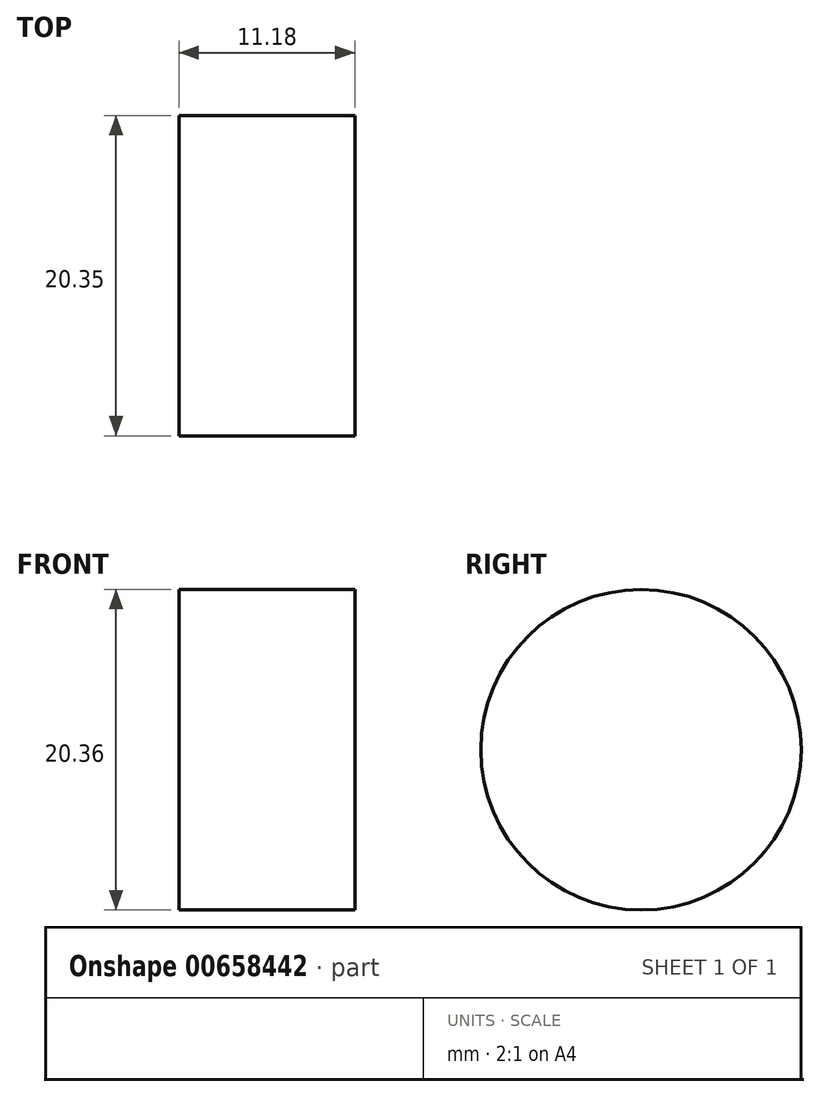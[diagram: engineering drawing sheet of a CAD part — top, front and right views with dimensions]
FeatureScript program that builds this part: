
annotation { "Feature Type Name" : "Feature", "Feature Type Description" : "" }
export const myFeature = defineFeature(function(context is Context, id is Id, definition is map)
    precondition{}
    {
        {
            var Q0;
            Q0=qCreatedBy(makeId("Right.planeOp"),FACE);
            var sketch = newSketch(context, id + "F0", { "sketchPlane" : qUnion([Q0])});
            skCircle(sketch, "E0", {"center": v(47.88, 10.4) * mm, "radius": 10.18 * mm});
            skSolve(sketch);
        }
        {
            var Q0;
            Q0 = qSketchRegion(id + "F0", true);
            extrude(context, id + "F1", {"entities" : qUnion([Q0]), "depth" : 11.18 * mm, "offsetDistance" : 25.4 * mm});
        }
        {
            var Q0;
            Q0=qCreatedBy(makeId("Right.planeOp"),FACE);
            var sketch = newSketch(context, id + "F2", { "sketchPlane" : qUnion([Q0])});
            skCircle(sketch, "E1", {"center": v(-41.59, 10.07) * mm, "radius": 10.04 * mm});
            skSolve(sketch);
        }
        {
            var Q0;
            Q0=makeQuery(id+"F2.imprint","IMPRINT",FACE,{"disambiguationData":[TD([[makeQuery(id+"F2.imprint","IMPRINT",EDGE,{"derivedFrom":sQuery(id+"F2.wireOp",EDGE,"E1")}),1.0]])]});
            extrude(context, id + "F3", {"entities" : qUnion([Q0]), "operationType" : NewBodyOperationType.ADD, "depth" : 11.18 * mm, "offsetDistance" : 25.4 * mm});
        }
        {
            var Q0;
            Q0=makeQuery(id+"F3.opExtrude","SWEPT_BODY",BODY,{"disambiguationData":[OSD([sQuery(id+"F2.wireOp",EDGE,"E1")])]});
            deleteBodies(context, id + "F4", {"entities" : qUnion([Q0])});
        }
    });
